FCSTD DOCUMENT  (FreeCAD 0.20R29603 (Git))
Label: Plafon
License: All rights reserved
LicenseURL: http://en.wikipedia.org/wiki/All_rights_reserved
objects: Sketcher::SketchObject×1, PartDesign::Body×1
note: 2 computed .brp shape members not serialized (recipe doc carries the construction recipe); baked Part::Feature solids carry a one-line shape summary decoded from their .brp

FEATURE [Sketcher::SketchObject] Sketch
  FullyConstrained = false
  MapMode = 5
  Support = -> [XY_Plane]
  sketch-geometry (12):
    g0: Circle CenterX=-20.4076 CenterY=8.70874 CenterZ=0 NormalX=0 NormalY=0 NormalZ=1 AngleXU=0 Radius=2.5
    g1: Circle CenterX=-20.4076 CenterY=28.7087 CenterZ=0 NormalX=0 NormalY=0 NormalZ=1 AngleXU=0 Radius=2.5
    g2: Circle CenterX=-20.4076 CenterY=18.7087 CenterZ=0 NormalX=0 NormalY=0 NormalZ=1 AngleXU=0 Radius=2.5
    g3: Circle CenterX=-10.4076 CenterY=18.7087 CenterZ=0 NormalX=0 NormalY=0 NormalZ=1 AngleXU=0 Radius=2.5
    g4: Circle CenterX=-30.4076 CenterY=18.7087 CenterZ=0 NormalX=0 NormalY=0 NormalZ=1 AngleXU=0 Radius=2.5
    g5: Circle CenterX=-26.0441 CenterY=41.4727 CenterZ=0 NormalX=0 NormalY=0 NormalZ=1 AngleXU=0 Radius=1.5
    g6: Circle CenterX=-14.2992 CenterY=41.4727 CenterZ=0 NormalX=0 NormalY=0 NormalZ=1 AngleXU=0 Radius=1.5
    g7: ArcOfCircle CenterX=-20.4076 CenterY=18.7087 CenterZ=0 NormalX=0 NormalY=0 NormalZ=1 AngleXU=0 Radius=20 StartAngle=2.0944 EndAngle=7.33038
    g8: LineSegment StartX=-30.4076 StartY=46.0293 StartZ=0 EndX=-10.4076 EndY=46.0293 EndZ=0
    g9: LineSegment StartX=-10.4076 StartY=46.0293 StartZ=0 EndX=-10.4076 EndY=36.0293 EndZ=0
    g10: LineSegment StartX=-10.4076 StartY=36.0293 StartZ=0 EndX=-30.4076 EndY=36.0293 EndZ=0
    g11: LineSegment StartX=-30.4076 StartY=36.0293 StartZ=0 EndX=-30.4076 EndY=46.0293 EndZ=0
  constraints (30):
    c: Diameter(g1) = 5
    c: Diameter(g0) = 5
    c: Diameter(g4) = 5
    c: Diameter(g2) = 5
    c: Diameter(g3) = 5
    c: Horizontal(g4,g2)
    c: Horizontal(g3,g2)
    c: Vertical(g1,g2)
    c: Vertical(g0,g2)
    c: Distance(g2,g1) = 10
    c: Distance(g2,g3) = 10
    c: Distance(g4,g2) = 10
    c: Distance(g0,g2) = 10
    c: Diameter(g6) = 3
    c: Diameter(g5) = 3
    c: Horizontal(g5,g6)
    c: Diameter(g7) = 40
    c: Coincident(g2,g7)
    c: Coincident(g8,g9)
    c: Coincident(g9,g10)
    c: Coincident(g10,g11)
    c: Coincident(g11,g8)
    c: Horizontal(g8)
    c: Horizontal(g10)
    c: Vertical(g9)
    c: Vertical(g11)
    c: DistanceX(g8,g8) = 20
    c: DistanceY(g11,g11) = 10
    c: Coincident(g7,g9)
    c: Coincident(g7,g10)
FEATURE [PartDesign::Body] Body
  Group = -> [Sketch]
  Origin = -> Origin
